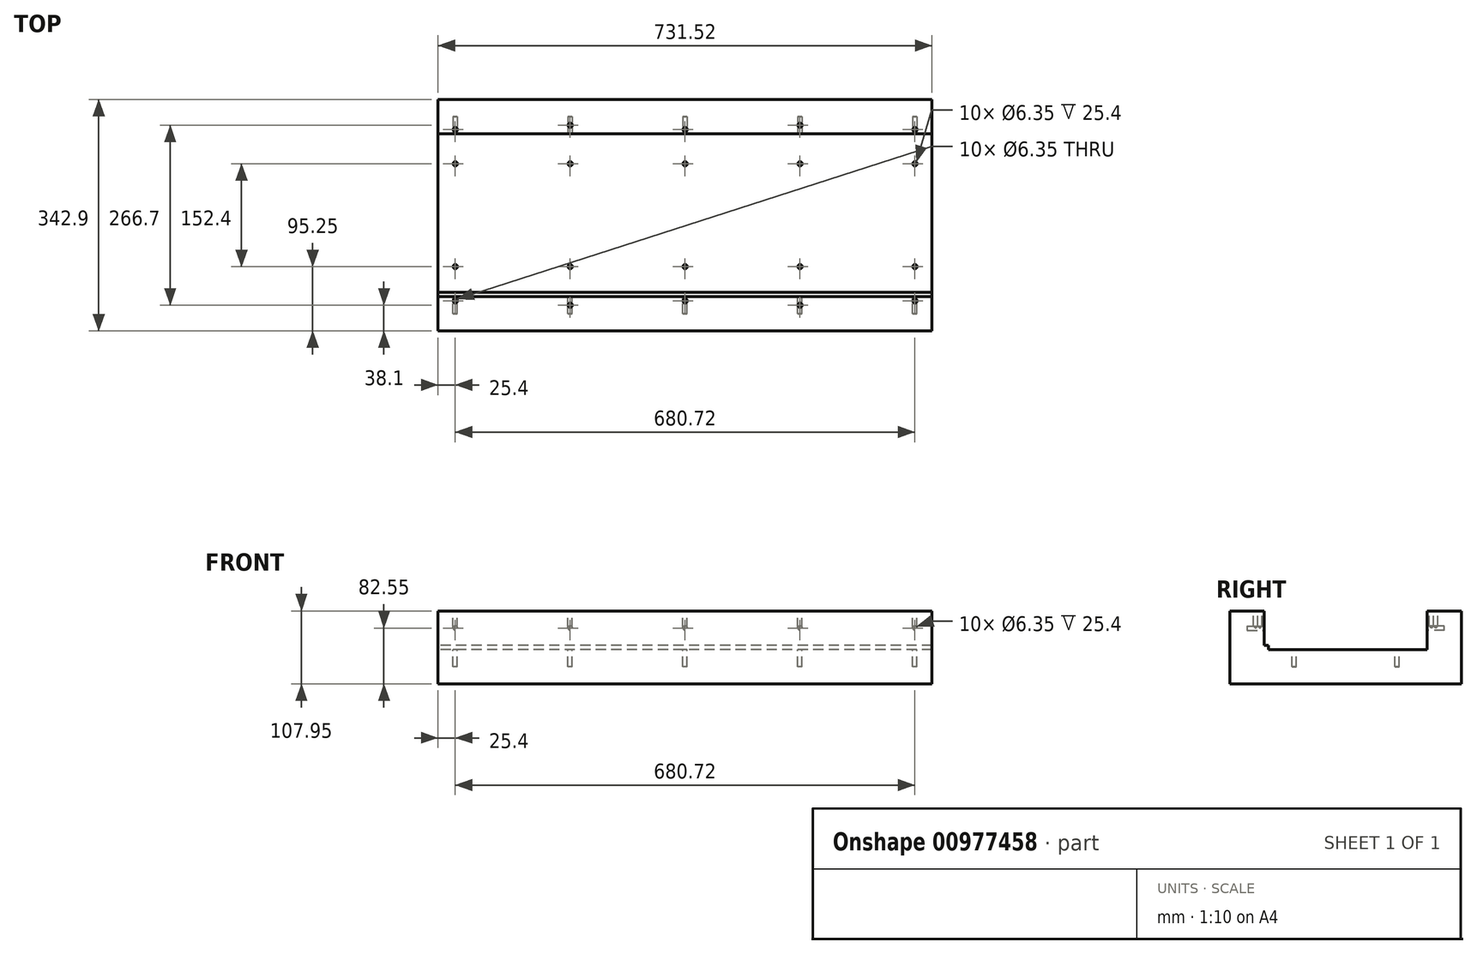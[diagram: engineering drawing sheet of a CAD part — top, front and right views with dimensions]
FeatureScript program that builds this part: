
annotation { "Feature Type Name" : "Feature", "Feature Type Description" : "" }
export const myFeature = defineFeature(function(context is Context, id is Id, definition is map)
    precondition{}
    {
        {
            var Q0;
            Q0=qCreatedBy(makeId("Right.planeOp"),FACE);
            var sketch = newSketch(context, id + "F0", { "sketchPlane" : qUnion([Q0])});
            skLineSegment(sketch, "E0", {"start": v(-171.45, 0) * mm, "end": v(171.45, 0) * mm});
            skLineSegment(sketch, "E1", {"start": v(171.45, 0) * mm, "end": v(171.45, 107.95) * mm});
            skLineSegment(sketch, "E2", {"start": v(-171.45, 0) * mm, "end": v(-171.45, 107.95) * mm});
            skLineSegment(sketch, "E3", {"start": v(-171.45, 107.95) * mm, "end": v(-120.65, 107.95) * mm});
            skLineSegment(sketch, "E4", {"start": v(-120.65, 107.95) * mm, "end": v(-120.65, 50.8) * mm});
            skLineSegment(sketch, "E5", {"start": v(-120.65, 50.8) * mm, "end": v(120.65, 50.8) * mm});
            skLineSegment(sketch, "E6", {"start": v(120.65, 50.8) * mm, "end": v(120.65, 107.95) * mm});
            skLineSegment(sketch, "E7", {"start": v(120.65, 107.95) * mm, "end": v(171.45, 107.95) * mm});
            skPoint(sketch, "E8", {"position": v(0, 50.8) * mm});
            skLineSegment(sketch, "E9.bottom", {"start": v(-120.65, 50.8) * mm, "end": v(-114.3, 50.8) * mm});
            skLineSegment(sketch, "E9.top", {"start": v(-120.65, 57.15) * mm, "end": v(-114.3, 57.15) * mm});
            skLineSegment(sketch, "E9.left", {"start": v(-120.65, 50.8) * mm, "end": v(-120.65, 57.15) * mm});
            skLineSegment(sketch, "E9.right", {"start": v(-114.3, 50.8) * mm, "end": v(-114.3, 57.15) * mm});
            skSolve(sketch);
        }
        {
            var Q0;
            Q0 = qSketchRegion(id + "F0", true);
            extrude(context, id + "F1", {"entities" : qUnion([Q0]), "endBound" : BoundingType.SYMMETRIC, "depth" : 731.52 * mm, "offsetDistance" : 25.4 * mm});
        }
        {
            var Q0;
            Q0=makeQuery(id+"F1.opExtrude","SWEPT_FACE",FACE,{"disambiguationData":[OSD([sQuery(id+"F0.wireOp",EDGE,"E5")])]});
            var sketch = newSketch(context, id + "F2", { "sketchPlane" : qUnion([Q0])});
            skCircle(sketch, "E10", {"center": v(170.18, -76.2) * mm, "radius": 3.18 * mm});
            skCircle(sketch, "E11", {"center": v(0, -76.2) * mm, "radius": 3.18 * mm});
            skCircle(sketch, "E12", {"center": v(-170.18, -76.2) * mm, "radius": 3.18 * mm});
            skCircle(sketch, "E13.MirrorC", {"center": v(0, 76.2) * mm, "radius": 3.18 * mm});
            skCircle(sketch, "E14.MirrorC", {"center": v(-170.18, 76.2) * mm, "radius": 3.18 * mm});
            skCircle(sketch, "E15.MirrorC", {"center": v(170.18, 76.2) * mm, "radius": 3.18 * mm});
            skCircle(sketch, "E16", {"center": v(-340.36, -76.2) * mm, "radius": 3.18 * mm});
            skCircle(sketch, "E17.MirrorC", {"center": v(340.36, -76.2) * mm, "radius": 3.18 * mm});
            skCircle(sketch, "E18.MirrorC", {"center": v(-340.36, 76.2) * mm, "radius": 3.18 * mm});
            skCircle(sketch, "E19.MirrorC", {"center": v(340.36, 76.2) * mm, "radius": 3.18 * mm});
            skSolve(sketch);
        }
        {
            var Q0;
            Q0 = qSketchRegion(id + "F2", true);
            extrude(context, id + "F3", {"entities" : qUnion([Q0]), "operationType" : NewBodyOperationType.REMOVE, "oppositeDirection" : true, "depth" : 25.4 * mm, "offsetDistance" : 25.4 * mm});
        }
        {
            var Q0;
            Q0=makeQuery(id+"F1.opExtrude","SWEPT_FACE",FACE,{"disambiguationData":[OSD([sQuery(id+"F0.wireOp",EDGE,"E6")])]});
            var sketch = newSketch(context, id + "F4", { "sketchPlane" : qUnion([Q0])});
            skCircle(sketch, "E20", {"center": v(0, 82.55) * mm, "radius": 3.18 * mm});
            skCircle(sketch, "E21", {"center": v(-170.18, 82.55) * mm, "radius": 3.18 * mm});
            skCircle(sketch, "E22", {"center": v(-340.36, 82.55) * mm, "radius": 3.18 * mm});
            skCircle(sketch, "E23.MirrorC", {"center": v(170.18, 82.55) * mm, "radius": 3.18 * mm});
            skCircle(sketch, "E24.MirrorC", {"center": v(340.36, 82.55) * mm, "radius": 3.18 * mm});
            skSolve(sketch);
        }
        {
            var Q0;
            Q0 = qSketchRegion(id + "F4", true);
            extrude(context, id + "F5", {"entities" : qUnion([Q0]), "operationType" : NewBodyOperationType.REMOVE, "oppositeDirection" : true, "depth" : 25.4 * mm, "offsetDistance" : 25.4 * mm});
        }
        {
            var Q0;
            Q0=makeQuery(id+"F1.opExtrude","SWEPT_FACE",FACE,{"disambiguationData":[OSD([sQuery(id+"F0.wireOp",EDGE,"E4")])]});
            var sketch = newSketch(context, id + "F6", { "sketchPlane" : qUnion([Q0])});
            skCircle(sketch, "E25", {"center": v(0, 82.55) * mm, "radius": 3.18 * mm});
            skCircle(sketch, "E26", {"center": v(-170.18, 82.55) * mm, "radius": 3.18 * mm});
            skCircle(sketch, "E27", {"center": v(-340.36, 82.55) * mm, "radius": 3.18 * mm});
            skCircle(sketch, "E28.MirrorC", {"center": v(170.18, 82.55) * mm, "radius": 3.18 * mm});
            skCircle(sketch, "E29.MirrorC", {"center": v(340.36, 82.55) * mm, "radius": 3.18 * mm});
            skSolve(sketch);
        }
        {
            var Q0;
            Q0 = qSketchRegion(id + "F6", true);
            extrude(context, id + "F7", {"entities" : qUnion([Q0]), "operationType" : NewBodyOperationType.REMOVE, "oppositeDirection" : true, "depth" : 25.4 * mm, "offsetDistance" : 25.4 * mm});
        }
        {
            var Q0;
            Q0=makeQuery(id+"F1.opExtrude","SWEPT_FACE",FACE,{"disambiguationData":[OSD([sQuery(id+"F0.wireOp",EDGE,"E3")])]});
            var sketch = newSketch(context, id + "F8", { "sketchPlane" : qUnion([Q0])});
            skCircle(sketch, "E30", {"center": v(0, -127) * mm, "radius": 3.18 * mm});
            skPoint(sketch, "E30.centerSnap0", {"position": v(0, -120.65) * mm});
            skCircle(sketch, "E31", {"center": v(-340.36, -127) * mm, "radius": 3.18 * mm});
            skCircle(sketch, "E32", {"center": v(-170.18, -133.35) * mm, "radius": 3.17 * mm});
            skCircle(sketch, "E33.MirrorC", {"center": v(170.18, -133.35) * mm, "radius": 3.17 * mm});
            skCircle(sketch, "E34.MirrorC", {"center": v(340.36, -127) * mm, "radius": 3.18 * mm});
            skCircle(sketch, "E35.MirrorC", {"center": v(-340.36, 127) * mm, "radius": 3.18 * mm});
            skCircle(sketch, "E36.MirrorC", {"center": v(-170.18, 133.35) * mm, "radius": 3.17 * mm});
            skCircle(sketch, "E37.MirrorC", {"center": v(0, 127) * mm, "radius": 3.18 * mm});
            skCircle(sketch, "E38.MirrorC", {"center": v(170.18, 133.35) * mm, "radius": 3.17 * mm});
            skCircle(sketch, "E39.MirrorC", {"center": v(340.36, 127) * mm, "radius": 3.18 * mm});
            skSolve(sketch);
        }
        {
            var Q0;
            Q0 = qSketchRegion(id + "F8", true);
            extrude(context, id + "F9", {"entities" : qUnion([Q0]), "operationType" : NewBodyOperationType.REMOVE, "oppositeDirection" : true, "depth" : 25.4 * mm, "offsetDistance" : 25.4 * mm});
        }
    });
